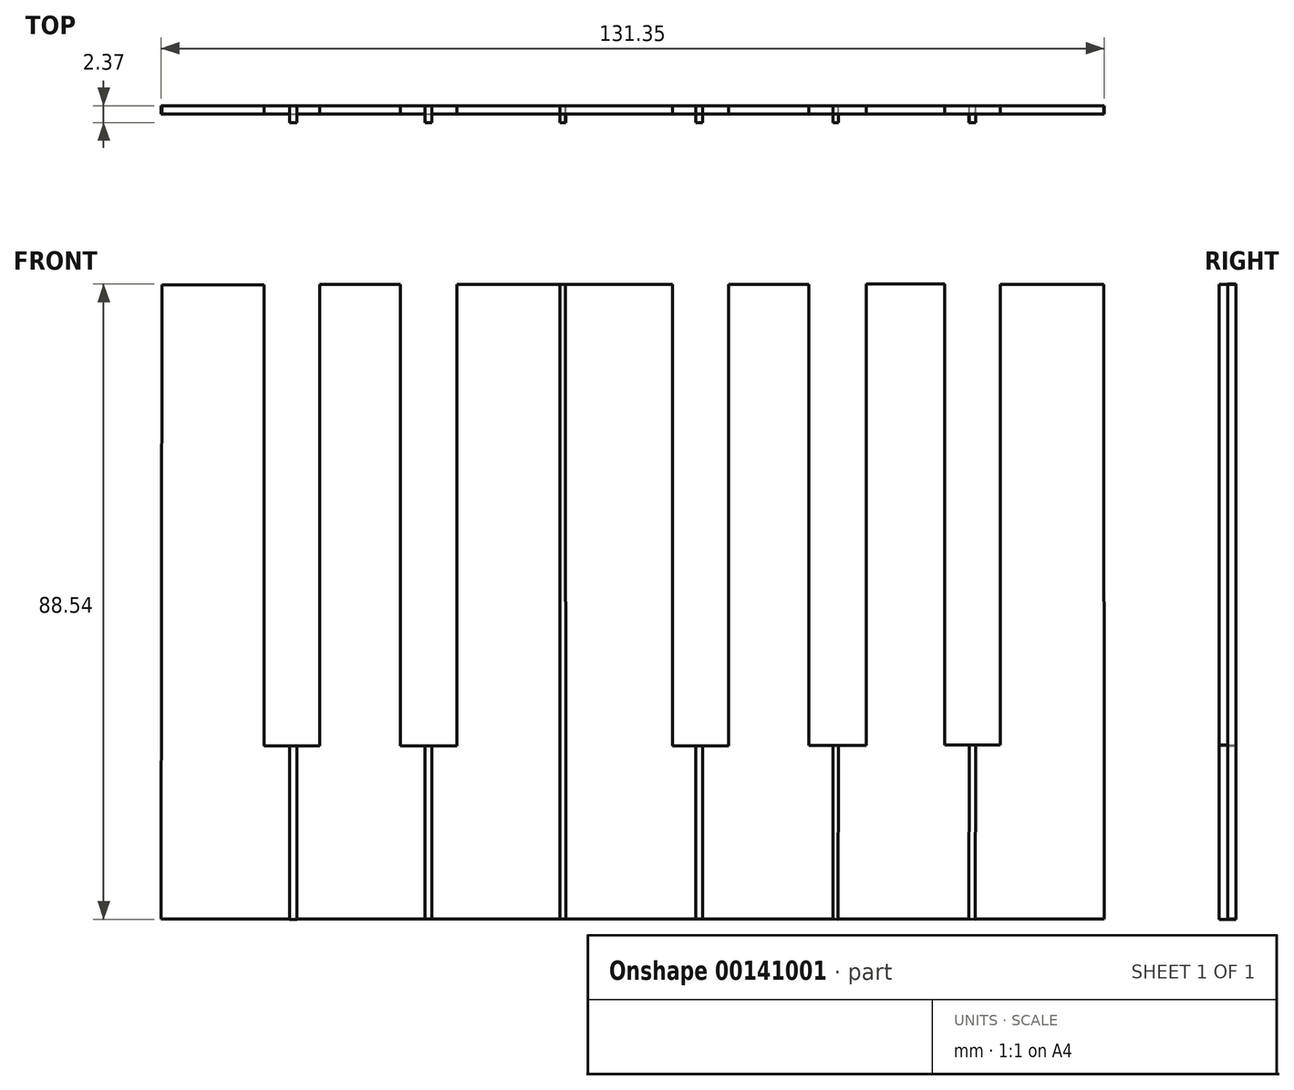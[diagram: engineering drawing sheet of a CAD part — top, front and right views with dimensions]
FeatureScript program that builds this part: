
annotation { "Feature Type Name" : "Feature", "Feature Type Description" : "" }
export const myFeature = defineFeature(function(context is Context, id is Id, definition is map)
    precondition{}
    {
        {
            var Q0;
            Q0=qCreatedBy(makeId("Front.planeOp"),FACE);
            var sketch = newSketch(context, id + "F0", { "sketchPlane" : qUnion([Q0])});
            skLineSegment(sketch, "E0", {"start": v(-69.25, 44.97) * mm, "end": v(63.45, 44.97) * mm});
            skLineSegment(sketch, "E1", {"start": v(63.45, 44.97) * mm, "end": v(63.45, -44.98) * mm});
            skLineSegment(sketch, "E2", {"start": v(63.45, -44.98) * mm, "end": v(-69.31, -44.93) * mm});
            skLineSegment(sketch, "E3", {"start": v(-69.31, -44.93) * mm, "end": v(-69.25, 44.97) * mm});
            skSolve(sketch);
        }
        {
            var Q0;
            Q0=makeQuery(id+"F0.imprint","IMPRINT",FACE,{"disambiguationData":[TD([[makeQuery(id+"F0.imprint","IMPRINT",EDGE,{"derivedFrom":sQuery(id+"F0.wireOp",EDGE,"E0")}),-1.0]])]});
            var sketch = newSketch(context, id + "F1", { "sketchPlane" : qUnion([Q0])});
            skLineSegment(sketch, "E4", {"start": v(-68.48, 44.15) * mm, "end": v(-54.27, 44.15) * mm});
            skLineSegment(sketch, "E5", {"start": v(-54.27, 44.15) * mm, "end": v(-54.27, -20.1) * mm});
            skLineSegment(sketch, "E6", {"start": v(-54.27, -20.1) * mm, "end": v(-46.54, -20.1) * mm});
            skLineSegment(sketch, "E7", {"start": v(-46.54, -20.1) * mm, "end": v(-46.54, 44.22) * mm});
            skLineSegment(sketch, "E8", {"start": v(-46.54, 44.22) * mm, "end": v(-35.3, 44.22) * mm});
            skLineSegment(sketch, "E9", {"start": v(-35.3, 44.22) * mm, "end": v(-35.3, -20.1) * mm});
            skLineSegment(sketch, "E10", {"start": v(-35.3, -20.1) * mm, "end": v(-27.4, -20.1) * mm});
            skLineSegment(sketch, "E11", {"start": v(-27.4, -20.1) * mm, "end": v(-27.4, 44.23) * mm});
            skLineSegment(sketch, "E12", {"start": v(-27.4, 44.23) * mm, "end": v(-13.07, 44.23) * mm});
            skLineSegment(sketch, "E13", {"start": v(-13.07, 44.23) * mm, "end": v(2.58, 44.23) * mm});
            skLineSegment(sketch, "E14", {"start": v(2.58, 44.23) * mm, "end": v(2.58, -20.06) * mm});
            skLineSegment(sketch, "E15", {"start": v(2.58, -20.06) * mm, "end": v(10.42, -20.06) * mm});
            skLineSegment(sketch, "E16", {"start": v(10.42, -20.06) * mm, "end": v(10.42, 44.23) * mm});
            skPoint(sketch, "E16.endSnap0", {"position": v(-5.24, 44.23) * mm});
            skLineSegment(sketch, "E17", {"start": v(10.42, 44.23) * mm, "end": v(21.62, 44.23) * mm});
            skLineSegment(sketch, "E18", {"start": v(21.62, 44.23) * mm, "end": v(21.62, -20) * mm});
            skLineSegment(sketch, "E19", {"start": v(21.62, -20) * mm, "end": v(29.57, -20) * mm});
            skLineSegment(sketch, "E20", {"start": v(29.57, -20) * mm, "end": v(29.57, 44.28) * mm});
            skLineSegment(sketch, "E21", {"start": v(29.57, 44.28) * mm, "end": v(40.51, 44.28) * mm});
            skLineSegment(sketch, "E22", {"start": v(40.51, 44.28) * mm, "end": v(40.51, -19.95) * mm});
            skLineSegment(sketch, "E23", {"start": v(40.51, -19.95) * mm, "end": v(48.3, -19.95) * mm});
            skLineSegment(sketch, "E24", {"start": v(48.3, -19.95) * mm, "end": v(48.3, 44.25) * mm});
            skLineSegment(sketch, "E25", {"start": v(48.3, 44.25) * mm, "end": v(62.66, 44.25) * mm});
            skLineSegment(sketch, "E26", {"start": v(62.66, 44.25) * mm, "end": v(62.74, -44.25) * mm});
            skLineSegment(sketch, "E27", {"start": v(62.74, -44.25) * mm, "end": v(-68.6, -44.25) * mm});
            skLineSegment(sketch, "E28", {"start": v(-68.6, -44.25) * mm, "end": v(-68.48, 44.15) * mm});
            skSolve(sketch);
        }
        {
            var Q0;
            Q0=makeQuery(id+"F1.imprint","IMPRINT",FACE,{"disambiguationData":[TD([[makeQuery(id+"F1.imprint","IMPRINT",EDGE,{"derivedFrom":sQuery(id+"F1.wireOp",EDGE,"E4")}),-1.0]])]});
            var sketch = newSketch(context, id + "F2", { "sketchPlane" : qUnion([Q0])});
            skLineSegment(sketch, "E29", {"start": v(-50.73, -20.1) * mm, "end": v(-50.73, -44.25) * mm});
            skLineSegment(sketch, "E30", {"start": v(-50.73, -44.25) * mm, "end": v(-49.74, -44.25) * mm});
            skLineSegment(sketch, "E31", {"start": v(-49.74, -44.25) * mm, "end": v(-49.74, -20.08) * mm});
            skLineSegment(sketch, "E32", {"start": v(-49.74, -20.08) * mm, "end": v(-50.73, -20.1) * mm});
            skLineSegment(sketch, "E33", {"start": v(-31.9, -20.1) * mm, "end": v(-31.9, -44.25) * mm});
            skLineSegment(sketch, "E34", {"start": v(-31.9, -44.25) * mm, "end": v(-30.94, -44.25) * mm});
            skLineSegment(sketch, "E35", {"start": v(-30.94, -44.25) * mm, "end": v(-30.94, -20.1) * mm});
            skLineSegment(sketch, "E36", {"start": v(-30.94, -20.1) * mm, "end": v(-31.9, -20.1) * mm});
            skLineSegment(sketch, "E37", {"start": v(5.85, -20.06) * mm, "end": v(5.85, -44.25) * mm});
            skLineSegment(sketch, "E38", {"start": v(5.85, -44.25) * mm, "end": v(6.84, -44.25) * mm});
            skLineSegment(sketch, "E39", {"start": v(6.84, -44.25) * mm, "end": v(6.84, -20.06) * mm});
            skLineSegment(sketch, "E40", {"start": v(6.84, -20.06) * mm, "end": v(5.85, -20.06) * mm});
            skSolve(sketch);
        }
        {
            var Q0;
            Q0=makeQuery(id+"F1.imprint","IMPRINT",FACE,{"disambiguationData":[TD([[makeQuery(id+"F1.imprint","IMPRINT",EDGE,{"derivedFrom":sQuery(id+"F1.wireOp",EDGE,"E4")}),-1.0]])]});
            var sketch = newSketch(context, id + "F3", { "sketchPlane" : qUnion([Q0])});
            skLineSegment(sketch, "E41", {"start": v(24.94, -44.25) * mm, "end": v(24.97, -20) * mm});
            skLineSegment(sketch, "E42", {"start": v(24.97, -20) * mm, "end": v(25.72, -20) * mm});
            skLineSegment(sketch, "E43", {"start": v(25.72, -20) * mm, "end": v(25.68, -44.26) * mm});
            skLineSegment(sketch, "E44", {"start": v(25.68, -44.26) * mm, "end": v(24.94, -44.25) * mm});
            skLineSegment(sketch, "E45", {"start": v(43.89, -44.25) * mm, "end": v(43.93, -19.95) * mm});
            skLineSegment(sketch, "E46", {"start": v(43.93, -19.95) * mm, "end": v(44.82, -19.95) * mm});
            skLineSegment(sketch, "E47", {"start": v(44.82, -19.95) * mm, "end": v(44.78, -44.25) * mm});
            skLineSegment(sketch, "E48", {"start": v(44.78, -44.25) * mm, "end": v(43.89, -44.25) * mm});
            skSolve(sketch);
        }
        {
            var Q0;
            Q0=makeQuery(id+"F1.imprint","IMPRINT",FACE,{"disambiguationData":[TD([[makeQuery(id+"F1.imprint","IMPRINT",EDGE,{"derivedFrom":sQuery(id+"F1.wireOp",EDGE,"E4")}),-1.0]])]});
            var sketch = newSketch(context, id + "F4", { "sketchPlane" : qUnion([Q0])});
            skLineSegment(sketch, "E49", {"start": v(-13.08, 44.23) * mm, "end": v(-13.08, -44.25) * mm});
            skLineSegment(sketch, "E50", {"start": v(-13.08, -44.25) * mm, "end": v(-12.26, -44.25) * mm});
            skLineSegment(sketch, "E51", {"start": v(-12.26, -44.25) * mm, "end": v(-12.33, 44.22) * mm});
            skLineSegment(sketch, "E52", {"start": v(-12.33, 44.22) * mm, "end": v(-13.08, 44.23) * mm});
            skSolve(sketch);
        }
        {
            var Q0;
            Q0 = qSketchRegion(id + "F4", true);
            var Q1;
            Q1 = qSketchRegion(id + "F3", true);
            var Q2;
            Q2 = qSketchRegion(id + "F2", true);
            extrude(context, id + "F5", {"entities" : qUnion([Q0, Q1, Q2]), "depth" : 2.37 * mm});
        }
        {
            var Q0;
            Q0 = qSketchRegion(id + "F1", true);
            extrude(context, id + "F6", {"entities" : qUnion([Q0]), "depth" : 1.15 * mm});
        }
    });
